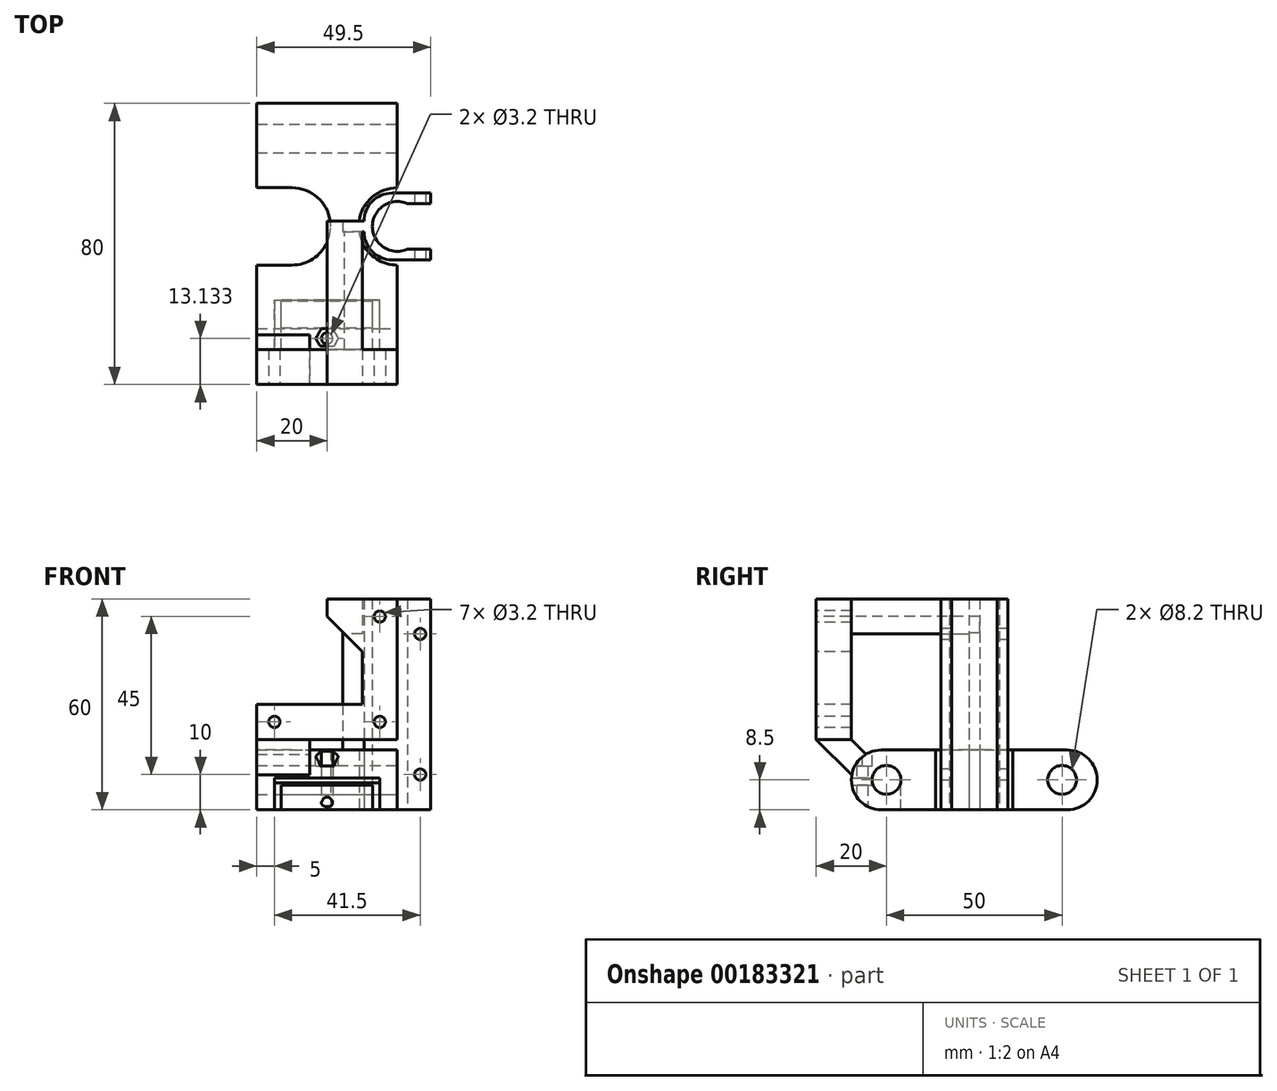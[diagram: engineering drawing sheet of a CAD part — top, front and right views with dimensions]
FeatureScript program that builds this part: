
annotation { "Feature Type Name" : "Feature", "Feature Type Description" : "" }
export const myFeature = defineFeature(function(context is Context, id is Id, definition is map)
    precondition{}
    {
        {
            var Q0;
            Q0=qCreatedBy(makeId("Front.planeOp"),FACE);
            cPlane(context, id + "F0", {"entities" : qUnion([Q0]), "cplaneType" : CPlaneType.OFFSET, "offset" : 21 * mm, "width" : 150 * mm, "height" : 150 * mm});
        }
        {
            var Q0;
            Q0=qCreatedBy(makeId("Right.planeOp"),FACE);
            var sketch = newSketch(context, id + "F1", { "sketchPlane" : qUnion([Q0])});
            skLineSegment(sketch, "E0.bottom", {"start": v(-26.5, 0) * mm, "end": v(26.5, 0) * mm});
            skLineSegment(sketch, "E0.top", {"start": v(-26.5, 17) * mm, "end": v(26.5, 17) * mm});
            skLineSegment(sketch, "E0.left", {"start": v(-35, 8.5) * mm, "end": v(-35, 8.5) * mm});
            skLineSegment(sketch, "E0.right", {"start": v(35, 8.5) * mm, "end": v(35, 8.5) * mm});
            skPoint(sketch, "E1.visualSharp", {"position": v(35, 17) * mm});
            skArc(sketch, "E1.filletArc", {"start": v(35, 8.5) * mm, "mid": v(32.51, 14.51) * mm, "end": v(26.5, 17) * mm});
            skPoint(sketch, "E2.visualSharp", {"position": v(35, 0) * mm});
            skArc(sketch, "E2.filletArc", {"start": v(26.5, 0) * mm, "mid": v(32.51, 2.49) * mm, "end": v(35, 8.5) * mm});
            skPoint(sketch, "E3.visualSharp", {"position": v(-35, 0) * mm});
            skArc(sketch, "E3.filletArc", {"start": v(-35, 8.5) * mm, "mid": v(-32.51, 2.49) * mm, "end": v(-26.5, 0) * mm});
            skPoint(sketch, "E4.visualSharp", {"position": v(-35, 17) * mm});
            skArc(sketch, "E4.filletArc", {"start": v(-26.5, 17) * mm, "mid": v(-32.51, 14.51) * mm, "end": v(-35, 8.5) * mm});
            skCircle(sketch, "E5", {"center": v(-25, 8.5) * mm, "radius": 4.1 * mm});
            skCircle(sketch, "E6", {"center": v(25, 8.5) * mm, "radius": 4.1 * mm});
            skSolve(sketch);
        }
        {
            var Q0;
            Q0 = qSketchRegion(id + "F1", true);
            extrude(context, id + "F2", {"entities" : qUnion([Q0]), "oppositeDirection" : true, "depth" : 40 * mm});
        }
        {
            var Q0;
            Q0=qCreatedBy(makeId("Top.planeOp"),FACE);
            var sketch = newSketch(context, id + "F3", { "sketchPlane" : qUnion([Q0])});
            skCircle(sketch, "E7", {"center": v(0, 0) * mm, "radius": 11 * mm});
            skSolve(sketch);
        }
        {
            var Q0;
            Q0 = qSketchRegion(id + "F3", true);
            extrude(context, id + "F4", {"entities" : qUnion([Q0]), "operationType" : NewBodyOperationType.REMOVE, "depth" : 17 * mm});
        }
        {
            var Q0;
            Q0=qCreatedBy(makeId("Top.planeOp"),FACE);
            var sketch = newSketch(context, id + "F5", { "sketchPlane" : qUnion([Q0])});
            skLineSegment(sketch, "E8.bottom", {"start": v(9.5, 9.5) * mm, "end": v(-1.5, 9.5) * mm});
            skLineSegment(sketch, "E8.top", {"start": v(9.5, -9.5) * mm, "end": v(-1.5, -9.5) * mm});
            skLineSegment(sketch, "E8.left", {"start": v(9.5, 9.5) * mm, "end": v(9.5, -9.5) * mm});
            skLineSegment(sketch, "E8.right", {"start": v(-9.5, 1.5) * mm, "end": v(-9.5, -1.5) * mm});
            skPoint(sketch, "E8.middle", {"position": v(0, 0) * mm});
            skPoint(sketch, "E9.visualSharp", {"position": v(-9.5, 9.5) * mm});
            skArc(sketch, "E9.filletArc", {"start": v(-1.5, 9.5) * mm, "mid": v(-7.16, 7.16) * mm, "end": v(-9.5, 1.5) * mm});
            skPoint(sketch, "E10.visualSharp", {"position": v(-9.5, -9.5) * mm});
            skArc(sketch, "E10.filletArc", {"start": v(-9.5, -1.5) * mm, "mid": v(-7.16, -7.16) * mm, "end": v(-1.5, -9.5) * mm});
            skCircle(sketch, "E11", {"center": v(0, 0) * mm, "radius": 7.1 * mm});
            skLineSegment(sketch, "E12.bottom", {"start": v(9.5, -6.5) * mm, "end": v(2.86, -6.5) * mm});
            skLineSegment(sketch, "E12.top", {"start": v(9.5, 6.5) * mm, "end": v(2.86, 6.5) * mm});
            skLineSegment(sketch, "E12.left", {"start": v(9.5, -6.5) * mm, "end": v(9.5, 6.5) * mm});
            skLineSegment(sketch, "E13.bottom", {"start": v(-15.5, 1.5) * mm, "end": v(-9.5, 1.5) * mm});
            skLineSegment(sketch, "E13.top", {"start": v(-15.5, -1.5) * mm, "end": v(-9.5, -1.5) * mm});
            skLineSegment(sketch, "E13.left", {"start": v(-15.5, 1.5) * mm, "end": v(-15.5, -1.5) * mm});
            skSolve(sketch);
        }
        {
            var Q0;
            {var subQ4=sQuery(id+"F5.wireOp",EDGE,"E8.bottom");Q0=makeQuery(id+"F5.imprint","IMPRINT",FACE,{"disambiguationData":[TD([[makeQuery(id+"F5.imprint","IMPRINT",EDGE,{"derivedFrom":subQ4}),1.0]])]});}
            var Q1;
            Q1=makeQuery(id+"F5.imprint","IMPRINT",FACE,{"disambiguationData":[TD([[makeQuery(id+"F5.imprint","IMPRINT",EDGE,{"derivedFrom":sQuery(id+"F5.wireOp",EDGE,"E13.bottom")}),-1.0]])]});
            extrude(context, id + "F6", {"entities" : qUnion([Q0, Q1]), "operationType" : NewBodyOperationType.ADD, "depth" : 60 * mm});
        }
        {
            var Q0;
            Q0=makeQuery(id+"F6.opExtrude","SWEPT_FACE",FACE,{"disambiguationData":[OSD([sQuery(id+"F5.wireOp",EDGE,"E8.top")])]});
            var sketch = newSketch(context, id + "F7", { "sketchPlane" : qUnion([Q0])});
            skCircle(sketch, "E14", {"center": v(6.5, 50) * mm, "radius": 1.6 * mm});
            skCircle(sketch, "E15", {"center": v(6.5, 10) * mm, "radius": 1.6 * mm});
            skSolve(sketch);
        }
        {
            var Q0;
            Q0 = qSketchRegion(id + "F7", true);
            extrude(context, id + "F8", {"entities" : qUnion([Q0]), "operationType" : NewBodyOperationType.REMOVE, "oppositeDirection" : true, "depth" : 19 * mm});
        }
        {
            var Q0;
            Q0=qCreatedBy(makeId("Top.planeOp"),FACE);
            var sketch = newSketch(context, id + "F9", { "sketchPlane" : qUnion([Q0])});
            skLineSegment(sketch, "E16.bottom", {"start": v(-30, 11) * mm, "end": v(-41, 11) * mm});
            skLineSegment(sketch, "E16.top", {"start": v(-30, -11) * mm, "end": v(-41, -11) * mm});
            skLineSegment(sketch, "E16.left", {"start": v(-19, 0) * mm, "end": v(-19, 0) * mm});
            skLineSegment(sketch, "E16.right", {"start": v(-41, 11) * mm, "end": v(-41, -11) * mm});
            skPoint(sketch, "E16.middle", {"position": v(-30, 0) * mm});
            skPoint(sketch, "E17.visualSharp", {"position": v(-19, -11) * mm});
            skArc(sketch, "E17.filletArc", {"start": v(-30, -11) * mm, "mid": v(-22.22, -7.78) * mm, "end": v(-19, 0) * mm});
            skPoint(sketch, "E18.visualSharp", {"position": v(-19, 11) * mm});
            skArc(sketch, "E18.filletArc", {"start": v(-19, 0) * mm, "mid": v(-22.22, 7.78) * mm, "end": v(-30, 11) * mm});
            skSolve(sketch);
        }
        {
            var Q0;
            Q0 = qSketchRegion(id + "F9", true);
            extrude(context, id + "F10", {"entities" : qUnion([Q0]), "operationType" : NewBodyOperationType.REMOVE, "depth" : 17 * mm});
        }
        {
            var Q0;
            Q0=qCreatedBy(id+"F0.planeOp",FACE);
            var sketch = newSketch(context, id + "F11", { "sketchPlane" : qUnion([Q0])});
            skLineSegment(sketch, "E19.bottom", {"start": v(-5, 7) * mm, "end": v(-35, 7) * mm});
            skLineSegment(sketch, "E19.top", {"start": v(-5, 9) * mm, "end": v(-35, 9) * mm});
            skLineSegment(sketch, "E19.left", {"start": v(-5, 7) * mm, "end": v(-5, 9) * mm});
            skLineSegment(sketch, "E19.right", {"start": v(-35, 7) * mm, "end": v(-35, 9) * mm});
            skPoint(sketch, "E20", {"position": v(-35, 8) * mm});
            skLineSegment(sketch, "E21.bottom", {"start": v(-35, 9) * mm, "end": v(-33, 9) * mm});
            skLineSegment(sketch, "E21.top", {"start": v(-35, 0) * mm, "end": v(-33, 0) * mm});
            skLineSegment(sketch, "E21.left", {"start": v(-35, 9) * mm, "end": v(-35, 0) * mm});
            skLineSegment(sketch, "E21.right", {"start": v(-33, 9) * mm, "end": v(-33, 0) * mm});
            skLineSegment(sketch, "E22.bottom", {"start": v(-5, 9) * mm, "end": v(-7, 9) * mm});
            skLineSegment(sketch, "E22.top", {"start": v(-5, 0) * mm, "end": v(-7, 0) * mm});
            skLineSegment(sketch, "E22.left", {"start": v(-5, 9) * mm, "end": v(-5, 0) * mm});
            skLineSegment(sketch, "E22.right", {"start": v(-7, 9) * mm, "end": v(-7, 0) * mm});
            skSolve(sketch);
        }
        {
            var Q0;
            {var subQ5=sQuery(id+"F11.wireOp",EDGE,"E22.top");Q0=makeQuery(id+"F11.imprint","IMPRINT",FACE,{"disambiguationData":[TD([[makeQuery(id+"F11.imprint","IMPRINT",EDGE,{"derivedFrom":subQ5}),-1.0]])]});}
            var Q1;
            {var subQ5=sQuery(id+"F11.wireOp",EDGE,"E22.bottom");Q1=makeQuery(id+"F11.imprint","IMPRINT",FACE,{"disambiguationData":[TD([[makeQuery(id+"F11.imprint","IMPRINT",EDGE,{"derivedFrom":subQ5}),1.0]])]});}
            var Q2;
            {var subQ5=sQuery(id+"F11.wireOp",EDGE,"E19.top");Q2=makeQuery(id+"F11.imprint","IMPRINT",FACE,{"disambiguationData":[TD([[makeQuery(id+"F11.imprint","IMPRINT",EDGE,{"derivedFrom":subQ5}),1.0]])]});}
            var Q3;
            {var subQ5=sQuery(id+"F11.wireOp",EDGE,"E21.bottom");Q3=makeQuery(id+"F11.imprint","IMPRINT",FACE,{"disambiguationData":[TD([[makeQuery(id+"F11.imprint","IMPRINT",EDGE,{"derivedFrom":subQ5}),-1.0]])]});}
            var Q4;
            {var subQ5=sQuery(id+"F11.wireOp",EDGE,"E21.top");Q4=makeQuery(id+"F11.imprint","IMPRINT",FACE,{"disambiguationData":[TD([[makeQuery(id+"F11.imprint","IMPRINT",EDGE,{"derivedFrom":subQ5}),1.0]])]});}
            extrude(context, id + "F12", {"entities" : qUnion([Q0, Q1, Q2, Q3, Q4]), "operationType" : NewBodyOperationType.REMOVE, "depth" : 15 * mm});
        }
        {
            var Q0;
            Q0=qCreatedBy(makeId("Top.planeOp"),FACE);
            var sketch = newSketch(context, id + "F13", { "sketchPlane" : qUnion([Q0])});
            skCircle(sketch, "E23", {"center": v(-20, -31.87) * mm, "radius": 1.6 * mm});
            skLineSegment(sketch, "E24", {"start": v(-20, -31.87) * mm, "end": v(-20, -34.87) * mm, "construction": true});
            skSolve(sketch);
        }
        {
            var Q0;
            Q0=makeQuery(id+"F13.imprint","IMPRINT",FACE,{"disambiguationData":[TD([[makeQuery(id+"F13.imprint","IMPRINT",EDGE,{"derivedFrom":sQuery(id+"F13.wireOp",EDGE,"E23")}),1.0]])]});
            var Q1;
            Q1=sQuery(id+"F13.wireOp",EDGE,"E23");
            extrude(context, id + "F14", {"entities" : qUnion([Q0]), "operationType" : NewBodyOperationType.REMOVE, "surfaceEntities" : qUnion([Q1]), "depth" : 17 * mm});
        }
        {
            var Q0;
            Q0=makeQuery(id+"F2.opExtrude","SWEPT_FACE",FACE,{"disambiguationData":[OSD([sQuery(id+"F1.wireOp",EDGE,"E0.top")])]});
            var sketch = newSketch(context, id + "F15", { "sketchPlane" : qUnion([Q0])});
            skCircle(sketch, "E25.cCircle", {"center": v(-20, -31.87) * mm, "radius": 2.8 * mm, "construction": true});
            skLineSegment(sketch, "E25.0", {"start": v(-23.23, -31.87) * mm, "end": v(-21.62, -29.07) * mm});
            skLineSegment(sketch, "E25.1", {"start": v(-21.62, -29.07) * mm, "end": v(-18.38, -29.07) * mm});
            skLineSegment(sketch, "E25.2", {"start": v(-18.38, -29.07) * mm, "end": v(-16.77, -31.87) * mm});
            skLineSegment(sketch, "E25.3", {"start": v(-16.77, -31.87) * mm, "end": v(-18.38, -34.67) * mm});
            skLineSegment(sketch, "E25.4", {"start": v(-18.38, -34.67) * mm, "end": v(-21.62, -34.67) * mm});
            skLineSegment(sketch, "E25.5", {"start": v(-21.62, -34.67) * mm, "end": v(-23.23, -31.87) * mm});
            skPoint(sketch, "E25.0.midPoint", {"position": v(-22.42, -30.47) * mm});
            skSolve(sketch);
        }
        {
            var Q0;
            Q0=makeQuery(id+"F15.imprint","IMPRINT",FACE,{"disambiguationData":[TD([[makeQuery(id+"F15.imprint","IMPRINT",EDGE,{"derivedFrom":sQuery(id+"F15.wireOp",EDGE,"E25.0")}),-1.0]])]});
            extrude(context, id + "F16", {"entities" : qUnion([Q0]), "operationType" : NewBodyOperationType.REMOVE, "oppositeDirection" : true, "depth" : 4.5 * mm});
        }
        {
            var Q0;
            Q0=qCreatedBy(makeId("Front.planeOp"),FACE);
            cPlane(context, id + "F17", {"entities" : qUnion([Q0]), "cplaneType" : CPlaneType.OFFSET, "offset" : 45 * mm, "width" : 150 * mm, "height" : 150 * mm});
        }
        {
            var Q0;
            {var subQ0=sQuery(id+"F1.wireOp",EDGE,"E5");var subQ1=sQuery(id+"F1.wireOp",EDGE,"E4.filletArc");var subQ2=sQuery(id+"F1.wireOp",EDGE,"E3.filletArc");var subQ3=sQuery(id+"F1.wireOp",EDGE,"E0.top");var subQ4=sQuery(id+"F1.wireOp",EDGE,"E0.bottom");Q0=makeQuery(id+"F10.boolean.opBoolean","SPLIT",FACE,{"disambiguationData":[TD([makeQuery(id+"F2.opExtrude","SWEPT_FACE",FACE,{"disambiguationData":[OSD([subQ0])]})])],"derivedFrom":makeQuery(id+"F2.opExtrude","CAP_FACE",FACE,{"disambiguationData":[OSD([subQ4,subQ3,sQuery(id+"F1.wireOp",EDGE,"E1.filletArc"),sQuery(id+"F1.wireOp",EDGE,"E2.filletArc"),subQ2,subQ1,subQ0,sQuery(id+"F1.wireOp",EDGE,"E6")])],"isStart":false})});}
            var sketch = newSketch(context, id + "F18", { "sketchPlane" : qUnion([Q0])});
            skLineSegment(sketch, "E26", {"start": v(45, 20) * mm, "end": v(34.89, 9.89) * mm});
            skLineSegment(sketch, "E27", {"start": v(34.89, 9.89) * mm, "end": v(29.89, 14.89) * mm});
            skLineSegment(sketch, "E28", {"start": v(29.89, 14.89) * mm, "end": v(35, 20) * mm});
            skLineSegment(sketch, "E29", {"start": v(35, 20) * mm, "end": v(45, 20) * mm});
            skSolve(sketch);
        }
        {
            var Q0;
            Q0 = qSketchRegion(id + "F18", true);
            extrude(context, id + "F19", {"entities" : qUnion([Q0]), "operationType" : NewBodyOperationType.ADD, "oppositeDirection" : true, "depth" : 15 * mm});
        }
        {
            var Q0;
            Q0=qCreatedBy(makeId("Right.planeOp"),FACE);
            cPlane(context, id + "F20", {"entities" : qUnion([Q0]), "cplaneType" : CPlaneType.OFFSET, "offset" : 20 * mm, "oppositeDirection" : true, "width" : 150 * mm, "height" : 150 * mm});
        }
        {
            var Q0;
            Q0=qCreatedBy(id+"F17.planeOp",FACE);
            var sketch = newSketch(context, id + "F21", { "sketchPlane" : qUnion([Q0])});
            skLineSegment(sketch, "E30", {"start": v(0, 20) * mm, "end": v(-40, 20) * mm});
            skLineSegment(sketch, "E31", {"start": v(-40, 20) * mm, "end": v(-40, 30) * mm});
            skLineSegment(sketch, "E32", {"start": v(-40, 30) * mm, "end": v(-10, 30) * mm});
            skLineSegment(sketch, "E33", {"start": v(-10, 60) * mm, "end": v(0, 60) * mm});
            skLineSegment(sketch, "E34", {"start": v(0, 60) * mm, "end": v(0, 20) * mm});
            skCircle(sketch, "E35", {"center": v(-35, 25) * mm, "radius": 1.6 * mm});
            skCircle(sketch, "E36", {"center": v(-5, 25) * mm, "radius": 1.6 * mm});
            skCircle(sketch, "E37", {"center": v(-5, 55) * mm, "radius": 1.6 * mm});
            skPoint(sketch, "E37.centerSnap0", {"position": v(-5, 60) * mm});
            skLineSegment(sketch, "E38", {"start": v(-10, 60) * mm, "end": v(-20, 60) * mm});
            skLineSegment(sketch, "E39", {"start": v(-10, 45) * mm, "end": v(-10, 30) * mm});
            skLineSegment(sketch, "E40", {"start": v(-20, 60) * mm, "end": v(-20, 55) * mm});
            skLineSegment(sketch, "E41", {"start": v(-20, 55) * mm, "end": v(-10, 45) * mm});
            skSolve(sketch);
        }
        {
            var Q0;
            Q0 = qSketchRegion(id + "F21", true);
            extrude(context, id + "F22", {"entities" : qUnion([Q0]), "operationType" : NewBodyOperationType.ADD, "oppositeDirection" : true, "depth" : 10 * mm});
        }
        {
            var Q0;
            Q0=makeQuery(id+"FLtXl66FDAkBEvf_1.boolean.opBoolean","MERGE",FACE,{"derivedFrom":[makeQuery(id+"F6.opExtrude","SWEPT_FACE",FACE,{"disambiguationData":[OSD([sQuery(id+"F5.wireOp",EDGE,"E13.bottom")])]}),makeQuery(id+"FLtXl66FDAkBEvf_1.opExtrude","SWEPT_FACE",FACE,{"disambiguationData":[OSD([sQuery(id+"FSWC1r9MkEBXhsm_1.wireOp",EDGE,"xeegCUlc-6vyF-FMu4-Xd5Z-f3j3bLNUwnzt")])]})]});
            var sketch = newSketch(context, id + "F23", { "sketchPlane" : qUnion([Q0])});
            skLineSegment(sketch, "E42", {"start": v(10, 60) * mm, "end": v(10, 50) * mm});
            skLineSegment(sketch, "E43", {"start": v(10, 60) * mm, "end": v(20, 60) * mm});
            skLineSegment(sketch, "E44", {"start": v(20, 60) * mm, "end": v(20, 55) * mm});
            skLineSegment(sketch, "E45", {"start": v(10, 50) * mm, "end": v(15, 50) * mm});
            skLineSegment(sketch, "E46", {"start": v(15, 50) * mm, "end": v(20, 55) * mm});
            skSolve(sketch);
        }
        {
            var Q0;
            Q0 = qSketchRegion(id + "F23", true);
            extrude(context, id + "F24", {"entities" : qUnion([Q0]), "operationType" : NewBodyOperationType.ADD, "oppositeDirection" : true, "depth" : 46.5 * mm});
        }
    });
